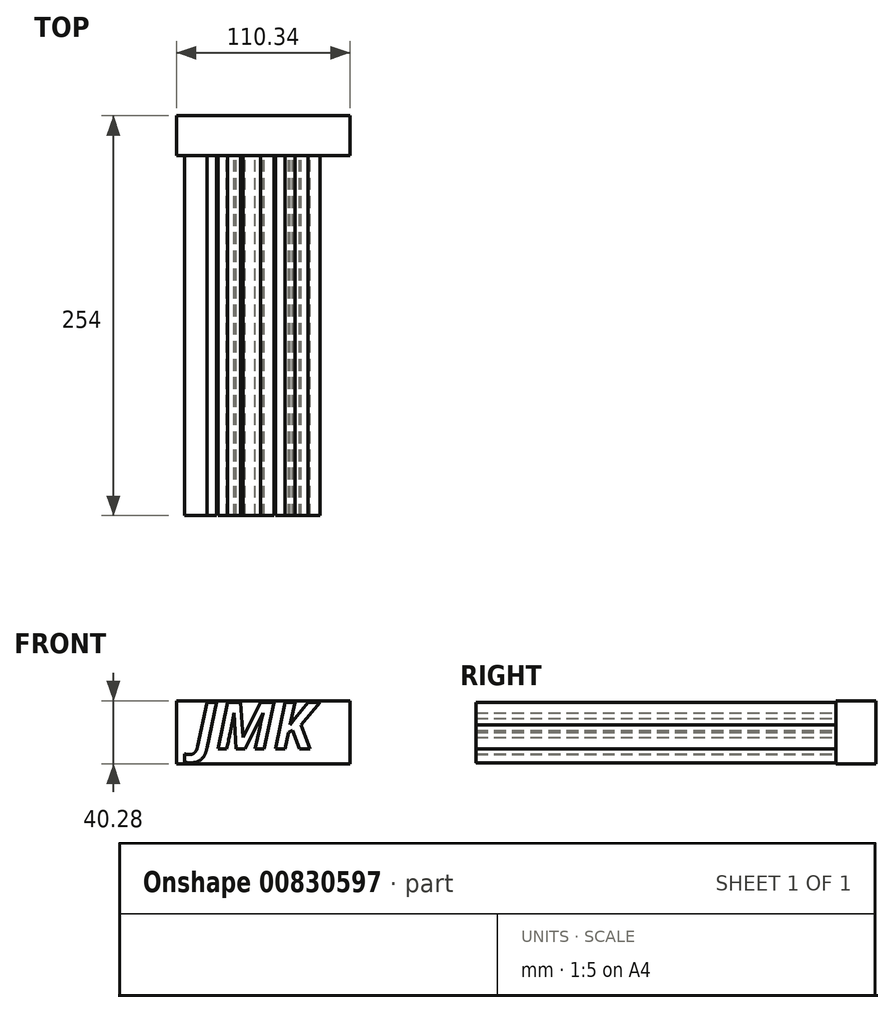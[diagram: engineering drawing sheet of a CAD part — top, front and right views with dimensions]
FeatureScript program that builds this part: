
annotation { "Feature Type Name" : "Feature", "Feature Type Description" : "" }
export const myFeature = defineFeature(function(context is Context, id is Id, definition is map)
    precondition{}
    {
        {
            var Q0;
            Q0=qCreatedBy(makeId("Front.planeOp"),FACE);
            var sketch = newSketch(context, id + "F0", { "sketchPlane" : qUnion([Q0])});
            skLineSegment(sketch, "E0.bottom", {"start": v(0, 40.28) * mm, "end": v(110.34, 40.28) * mm});
            skLineSegment(sketch, "E0.top", {"start": v(0, 0) * mm, "end": v(110.34, 0) * mm});
            skLineSegment(sketch, "E0.left", {"start": v(0, 40.28) * mm, "end": v(0, 0) * mm});
            skLineSegment(sketch, "E0.right", {"start": v(110.34, 40.28) * mm, "end": v(110.34, 0) * mm});
            skSolve(sketch);
        }
        {
            var Q0;
            Q0=makeQuery(id+"F0.imprint","IMPRINT",FACE,{"disambiguationData":[TD([[makeQuery(id+"F0.imprint","IMPRINT",EDGE,{"derivedFrom":sQuery(id+"F0.wireOp",EDGE,"E0.bottom")}),-1.0]])]});
            extrude(context, id + "F1", {"entities" : qUnion([Q0]), "depth" : 25.4 * mm, "offsetDistance" : 25.4 * mm});
        }
        {
            var Q0;
            Q0=qCreatedBy(makeId("Front.planeOp"),FACE);
            var sketch = newSketch(context, id + "F2", { "sketchPlane" : qUnion([Q0])});
            skText(sketch, "E1", { "text": "JMK", "fontName": "OpenSans-BoldItalic.ttf"});
            const initialGuessF2  = {"E1": [0.01163, 0.0095, 1, 0, 0.02987]};
            skSetInitialGuess(sketch, initialGuessF2);
            skSolve(sketch);
        }
        {
            var Q0;
            Q0 = qSketchRegion(id + "F2", true);
            extrude(context, id + "F3", {"entities" : qUnion([Q0]), "operationType" : NewBodyOperationType.ADD, "depth" : 25.4 * mm, "offsetDistance" : 25.4 * mm});
        }
        {
            var Q0;
            Q0 = qSketchRegion(id + "F2", true);
            extrude(context, id + "F4", {"entities" : qUnion([Q0]), "operationType" : NewBodyOperationType.ADD, "depth" : 25.4 * mm, "offsetDistance" : 25.4 * mm});
        }
        {
            var Q0;
            Q0 = qSketchRegion(id + "F2", true);
            extrude(context, id + "F5", {"entities" : qUnion([Q0]), "operationType" : NewBodyOperationType.ADD, "depth" : 254 * mm, "offsetDistance" : 25.4 * mm});
        }
    });
